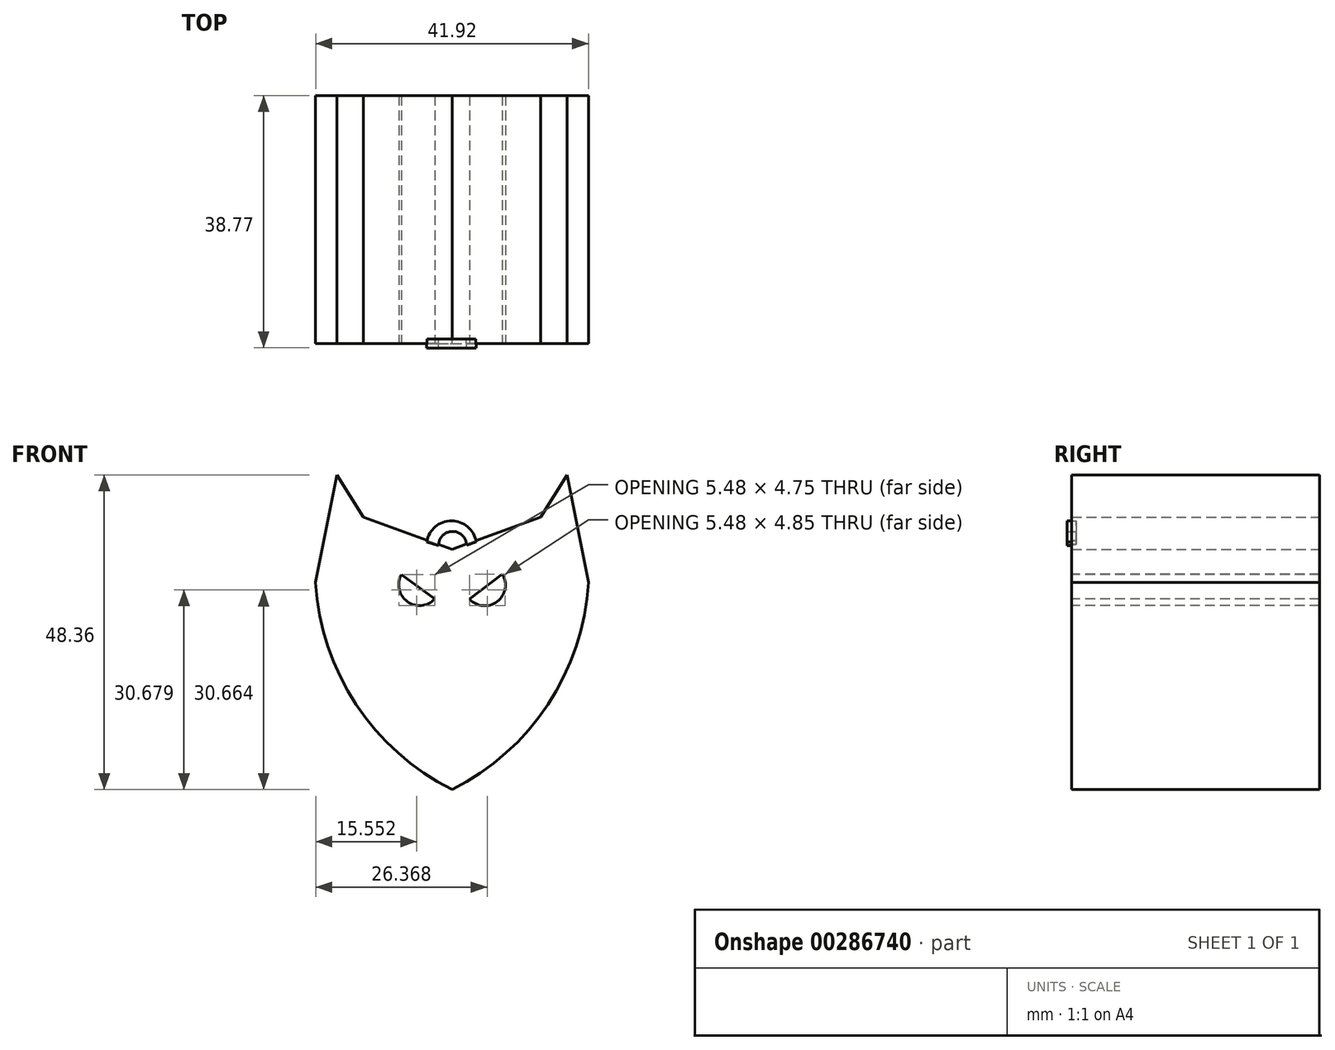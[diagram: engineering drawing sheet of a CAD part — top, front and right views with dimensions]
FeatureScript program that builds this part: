
annotation { "Feature Type Name" : "Feature", "Feature Type Description" : "" }
export const myFeature = defineFeature(function(context is Context, id is Id, definition is map)
    precondition{}
    {
        {
            var Q0;
            Q0=qCreatedBy(makeId("Front.planeOp"),FACE);
            var sketch = newSketch(context, id + "F0", { "sketchPlane" : qUnion([Q0])});
            skArc(sketch, "E0", {"start": v(-20.96, 16.56) * mm, "mid": v(-14.74, -2.15) * mm, "end": v(0, -15.25) * mm});
            skArc(sketch, "E1", {"start": v(0, -15.25) * mm, "mid": v(14.74, -2.15) * mm, "end": v(20.96, 16.56) * mm});
            skLineSegment(sketch, "E2", {"start": v(-20.96, 16.56) * mm, "end": v(-17.7, 33.1) * mm});
            skLineSegment(sketch, "E3", {"start": v(-17.7, 33.1) * mm, "end": v(-13.6, 26.62) * mm});
            skLineSegment(sketch, "E4", {"start": v(-13.6, 26.62) * mm, "end": v(0, 21.65) * mm});
            skLineSegment(sketch, "E5", {"start": v(0, 21.65) * mm, "end": v(13.6, 26.62) * mm});
            skLineSegment(sketch, "E6", {"start": v(13.6, 26.62) * mm, "end": v(17.7, 33.1) * mm});
            skLineSegment(sketch, "E7", {"start": v(17.7, 33.1) * mm, "end": v(20.96, 16.56) * mm});
            skSolve(sketch);
        }
        {
            var Q0;
            Q0=makeQuery(id+"F0.imprint","IMPRINT",FACE,{"disambiguationData":[TD([[makeQuery(id+"F0.imprint","IMPRINT",EDGE,{"derivedFrom":sQuery(id+"F0.wireOp",EDGE,"E0")}),1.0]])]});
            extrude(context, id + "F1", {"entities" : qUnion([Q0]), "depth" : 38.1 * mm});
        }
        {
            var Q0;
            Q0=makeQuery(id+"F1.opExtrude","CAP_FACE",FACE,{"disambiguationData":[OSD([sQuery(id+"F0.wireOp",EDGE,"E0"),sQuery(id+"F0.wireOp",EDGE,"E1"),sQuery(id+"F0.wireOp",EDGE,"E2"),sQuery(id+"F0.wireOp",EDGE,"E3"),sQuery(id+"F0.wireOp",EDGE,"E4"),sQuery(id+"F0.wireOp",EDGE,"E5"),sQuery(id+"F0.wireOp",EDGE,"E6"),sQuery(id+"F0.wireOp",EDGE,"E7")])],"isStart":false});
            var sketch = newSketch(context, id + "F2", { "sketchPlane" : qUnion([Q0])});
            skLineSegment(sketch, "E8", {"start": v(-7.78, 17.79) * mm, "end": v(-2.67, 14.02) * mm});
            skLineSegment(sketch, "E9", {"start": v(2.67, 14.02) * mm, "end": v(7.73, 17.86) * mm});
            skArc(sketch, "E10", {"start": v(2.67, 14.02) * mm, "mid": v(6.94, 13.64) * mm, "end": v(7.73, 17.86) * mm});
            skArc(sketch, "E11", {"start": v(-7.78, 17.79) * mm, "mid": v(-6.88, 13.65) * mm, "end": v(-2.67, 14.02) * mm});
            skSolve(sketch);
        }
        {
            var Q0;
            Q0=makeQuery(id+"F2.imprint","IMPRINT",FACE,{"disambiguationData":[TD([[makeQuery(id+"F2.imprint","IMPRINT",EDGE,{"derivedFrom":sQuery(id+"F2.wireOp",EDGE,"E9")}),-1.0]])]});
            var Q1;
            Q1=makeQuery(id+"F2.imprint","IMPRINT",FACE,{"disambiguationData":[TD([[makeQuery(id+"F2.imprint","IMPRINT",EDGE,{"derivedFrom":sQuery(id+"F2.wireOp",EDGE,"E8")}),-1.0]])]});
            extrude(context, id + "F3", {"entities" : qUnion([Q0, Q1]), "operationType" : NewBodyOperationType.REMOVE, "oppositeDirection" : true, "depth" : 38.1 * mm});
        }
        {
            var Q0;
            Q0=makeQuery(id+"F1.opExtrude","CAP_FACE",FACE,{"disambiguationData":[OSD([sQuery(id+"F0.wireOp",EDGE,"E0"),sQuery(id+"F0.wireOp",EDGE,"E1"),sQuery(id+"F0.wireOp",EDGE,"E2"),sQuery(id+"F0.wireOp",EDGE,"E3"),sQuery(id+"F0.wireOp",EDGE,"E4"),sQuery(id+"F0.wireOp",EDGE,"E5"),sQuery(id+"F0.wireOp",EDGE,"E6"),sQuery(id+"F0.wireOp",EDGE,"E7")])],"isStart":false});
            var sketch = newSketch(context, id + "F4", { "sketchPlane" : qUnion([Q0])});
            skArc(sketch, "E12", {"start": v(3.7, 22.81) * mm, "mid": v(-0.1, 26.03) * mm, "end": v(-3.88, 22.81) * mm});
            skArc(sketch, "E13", {"start": v(2.22, 22.3) * mm, "mid": v(0.04, 24.41) * mm, "end": v(-2.06, 22.23) * mm});
            skLineSegment(sketch, "E14", {"start": v(-3.88, 22.81) * mm, "end": v(-2.06, 22.23) * mm});
            skLineSegment(sketch, "E15", {"start": v(2.22, 22.3) * mm, "end": v(3.7, 22.81) * mm});
            skSolve(sketch);
        }
        {
            var Q0;
            {var subQ0=sQuery(id+"F4.wireOp",EDGE,"E12");Q0=makeQuery(id+"F4.imprint","IMPRINT",FACE,{"disambiguationData":[TD([[makeQuery(id+"F4.imprint","IMPRINT",EDGE,{"derivedFrom":subQ0}),1.0]])]});}
            extrude(context, id + "F5", {"entities" : qUnion([Q0]), "operationType" : NewBodyOperationType.ADD, "depth" : 0.67 * mm, "hasSecondDirection" : true, "secondDirectionOppositeDirection" : true, "secondDirectionDepth" : 0.69 * mm});
        }
    });
